# Revit family: S-tank_CT
name_source: partatom
category: Оборудование
units: mm (PartAtom-declared; Revit-internal decimal feet)

## family parameters
Всегда вертикально = Да
Классификация = Нет
На основе рабочей плоскости = Нет
Общий = Нет
При загрузке вырезать с полостями = Нет
Размер круглого соединителя = Использовать диаметр
Тип детали = Нормальный
Точка расчета площади = Нет

## types (9) — shared parameters
ADSK_URL документации изделия = http://s-tank.ru
ADSK_Группирование = Оборудование
ADSK_Единица измерения = шт.
ADSK_Завод-изготовитель = ООО “С-ТЭНК ВОТЕР ХИТЕРС”
ADSK_Наименование = Холодоаккумулятор
DN1 = 80 мм
DN2 = 15 мм
H4 = 185 мм
Reflex_item_color = <По категории>
VLeg_b = Да
VLeg_s = Нет
shrf = 18 мм
v = 50 мм
Разработка семейств = https://rubim.tech

## per-type parameters (varying)
| type | A | ADSK_Код изделия | ADSK_Масса | B | C | E | H | a | Диаметрсизоляцией |
| CT 300 | 125 мм | 2.8001 | 65 | 260 мм | 1310 мм | 180 мм | 1565 мм | 90 мм | 540 мм |
| CT 500 | 122 мм | 2.8002 | 87 | 255 мм | 1305 мм | 230 мм | 1565 мм | 115 мм | 690 мм |
| CT 750 | 117 мм | 2.8003 | 103 | 245 мм | 1295 мм | 277 мм | 1590 мм | 138 мм | 830 мм |
| CT 1000 | 117 мм | 2.8004 | 131 | 245 мм | 1870 мм | 277 мм | 2165 мм | 138 мм | 830 мм |
| CT 1200 | 177 мм | 2.8005 | 174 | 315 мм | 1615 мм | 330 мм | 1980 мм | 165 мм | 990 мм |
| CT 1500 | 177 мм | 2.8006 | 200 | 315 мм | 1965 мм | 330 мм | 2330 мм | 165 мм | 990 мм |
| CT 2000 | 250 мм | 2.8007 | 246 | 400 мм | 1700 мм | 420 мм | 2070 мм | 210 мм | 1260 мм |
| CT 3000 | 332 мм | 2.8009 | 450 | 515 мм | 1815 мм | 513 мм | 2315 мм | 257 мм | 1540 мм |
| CT 5000 | 332 мм | 2.8010 | 615 | 515 мм | 2565 мм | 513 мм | 3170 мм | 257 мм | 1540 мм |

note: column(s) folded — value = type name in every type: ADSK_Марка

## geometry (parser evidence)
native form markers: Extrusion x2, Sweep x1
no freeform markers — native parametric forms only
